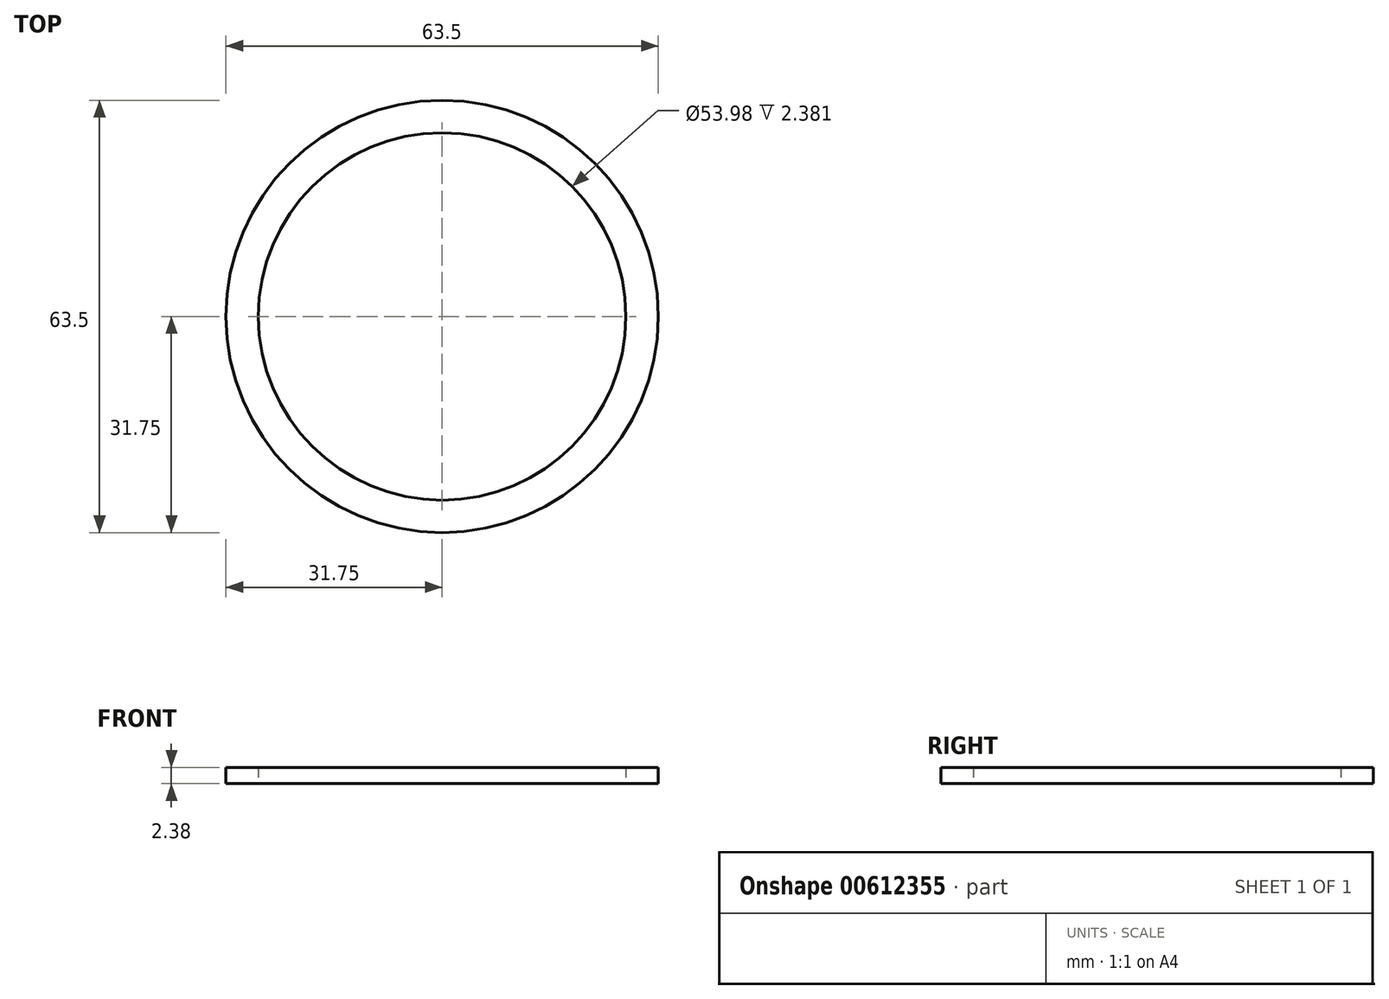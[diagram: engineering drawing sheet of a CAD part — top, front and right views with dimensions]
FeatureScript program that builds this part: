
annotation { "Feature Type Name" : "Feature", "Feature Type Description" : "" }
export const myFeature = defineFeature(function(context is Context, id is Id, definition is map)
    precondition{}
    {
        {
            var Q0;
            Q0=qCreatedBy(makeId("Front.planeOp"),FACE);
            var sketch = newSketch(context, id + "F0", { "sketchPlane" : qUnion([Q0])});
            skLineSegment(sketch, "E0.bottom", {"start": v(26.99, 0) * mm, "end": v(31.75, 0) * mm});
            skLineSegment(sketch, "E0.top", {"start": v(26.99, 2.38) * mm, "end": v(31.75, 2.38) * mm});
            skLineSegment(sketch, "E0.left", {"start": v(26.99, 0) * mm, "end": v(26.99, 2.38) * mm});
            skLineSegment(sketch, "E0.right", {"start": v(31.75, 0) * mm, "end": v(31.75, 2.38) * mm});
            skLineSegment(sketch, "E1", {"start": v(0, 0) * mm, "end": v(0, 17.15) * mm});
            skSolve(sketch);
        }
        {
            var Q0;
            Q0=makeQuery(id+"F0.imprint","IMPRINT",FACE,{"disambiguationData":[TD([[makeQuery(id+"F0.imprint","IMPRINT",EDGE,{"derivedFrom":sQuery(id+"F0.wireOp",EDGE,"E0.bottom")}),1.0]])]});
            var Q1;
            Q1=sQuery(id+"F0.wireOp",EDGE,"E1");
            revolve(context, id + "F1", {"entities" : qUnion([Q0]), "axis" : qUnion([Q1]), "revolveType" : RevolveType.FULL});
        }
    });
